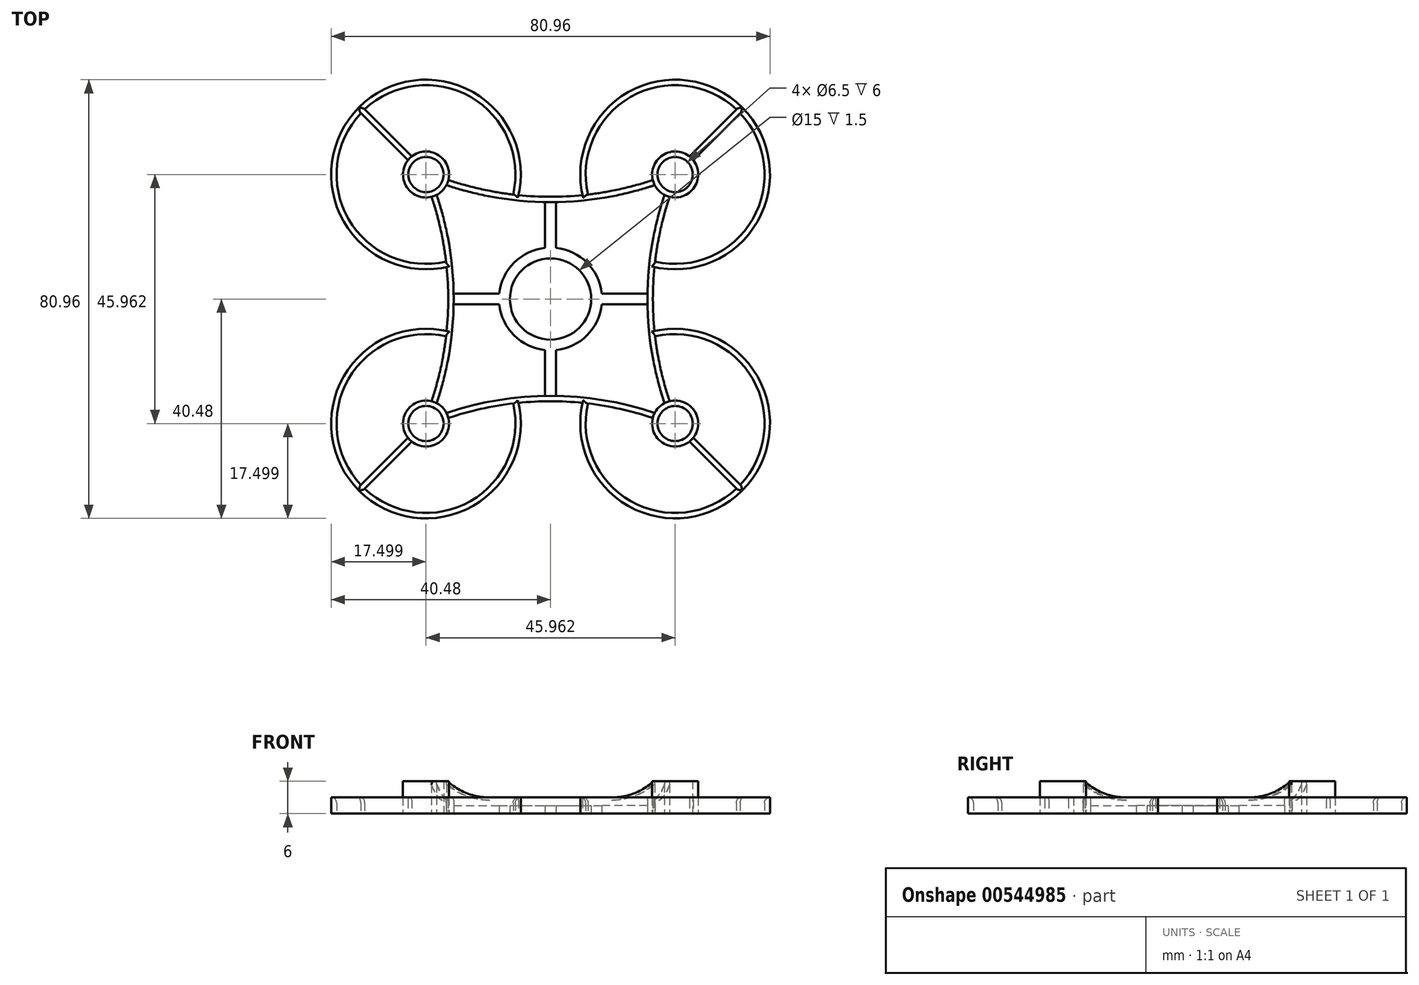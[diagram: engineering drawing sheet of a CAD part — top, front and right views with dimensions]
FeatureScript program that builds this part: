
annotation { "Feature Type Name" : "Feature", "Feature Type Description" : "" }
export const myFeature = defineFeature(function(context is Context, id is Id, definition is map)
    precondition{}
    {
        {
            var Q0;
            Q0=qCreatedBy(makeId("Top.planeOp"),FACE);
            var sketch = newSketch(context, id + "F0", { "sketchPlane" : qUnion([Q0])});
            skCircle(sketch, "E0", {"center": v(-22.98, 22.98) * mm, "radius": 3.25 * mm});
            skArc(sketch, "E1", {"start": v(-26.32, 25.61) * mm, "mid": v(-19.98, 19.98) * mm, "end": v(-25.61, 26.32) * mm});
            skLineSegment(sketch, "E2", {"start": v(0, 0) * mm, "end": v(-57.54, 57.54) * mm, "construction": true});
            skArc(sketch, "E3", {"start": v(-6.9, 19.28) * mm, "mid": v(-14.77, 37.3) * mm, "end": v(-34.29, 35) * mm});
            skArc(sketch, "E4", {"start": v(-5.9, 19.17) * mm, "mid": v(-35.36, 35.36) * mm, "end": v(-19.17, 5.9) * mm});
            skLineSegment(sketch, "E5", {"start": v(-18.38, 0) * mm, "end": v(-18.38, 18.38) * mm, "construction": true});
            skLineSegment(sketch, "E6", {"start": v(-18.38, 18.38) * mm, "end": v(0, 18.38) * mm, "construction": true});
            skArc(sketch, "E7", {"start": v(-18.38, 0) * mm, "mid": v(-19.54, 11.72) * mm, "end": v(-22.98, 22.98) * mm, "construction": true});
            skArc(sketch, "E8", {"start": v(-22.98, 22.98) * mm, "mid": v(-11.72, 19.54) * mm, "end": v(0, 18.37) * mm, "construction": true});
            skArc(sketch, "E9", {"start": v(-18.87, 0) * mm, "mid": v(-18.95, 2.95) * mm, "end": v(-19.17, 5.9) * mm});
            skArc(sketch, "E10", {"start": v(-17.88, 0) * mm, "mid": v(-18.67, 9.73) * mm, "end": v(-21.03, 19.2) * mm});
            skArc(sketch, "E11.MirrorCS", {"start": v(0, 18.87) * mm, "mid": v(-2.95, 18.95) * mm, "end": v(-5.9, 19.17) * mm});
            skArc(sketch, "E12.MirrorCS", {"start": v(0, 17.88) * mm, "mid": v(-9.73, 18.67) * mm, "end": v(-19.2, 21.03) * mm});
            skArc(sketch, "E13.trimOffspring", {"start": v(-6.9, 19.28) * mm, "mid": v(-12.95, 20.3) * mm, "end": v(-18.86, 21.96) * mm});
            skArc(sketch, "E14.trimOffspring", {"start": v(-19.28, 6.9) * mm, "mid": v(-20.3, 12.95) * mm, "end": v(-21.96, 18.86) * mm});
            skLineSegment(sketch, "E15", {"start": v(-35, 34.29) * mm, "end": v(-26.32, 25.61) * mm});
            skLineSegment(sketch, "E16.MirrorCS", {"start": v(-34.29, 35) * mm, "end": v(-25.61, 26.32) * mm});
            skArc(sketch, "E17.trimOffspring", {"start": v(-35, 34.29) * mm, "mid": v(-37.3, 14.77) * mm, "end": v(-19.28, 6.9) * mm});
            skLineSegment(sketch, "E18.MirrorCS", {"start": v(35, 34.29) * mm, "end": v(26.32, 25.61) * mm});
            skArc(sketch, "E19.MirrorCS", {"start": v(6.9, 19.28) * mm, "mid": v(12.95, 20.3) * mm, "end": v(18.86, 21.96) * mm});
            skArc(sketch, "E20.MirrorCS", {"start": v(19.28, 6.9) * mm, "mid": v(20.3, 12.95) * mm, "end": v(21.96, 18.86) * mm});
            skCircle(sketch, "E21.MirrorC", {"center": v(22.98, 22.98) * mm, "radius": 3.25 * mm});
            skArc(sketch, "E22.MirrorCS", {"start": v(26.32, 25.61) * mm, "mid": v(19.98, 19.98) * mm, "end": v(25.61, 26.32) * mm});
            skLineSegment(sketch, "E23.MirrorCS", {"start": v(0, 0) * mm, "end": v(57.54, 57.54) * mm, "construction": true});
            skArc(sketch, "E24.MirrorCS", {"start": v(5.9, 19.17) * mm, "mid": v(35.36, 35.36) * mm, "end": v(19.17, 5.9) * mm});
            skLineSegment(sketch, "E25.MirrorCS", {"start": v(18.38, 0) * mm, "end": v(18.38, 18.38) * mm, "construction": true});
            skLineSegment(sketch, "E26.MirrorCS", {"start": v(18.38, 18.38) * mm, "end": v(0, 18.38) * mm, "construction": true});
            skArc(sketch, "E27.MirrorCS", {"start": v(18.38, 0) * mm, "mid": v(19.54, 11.72) * mm, "end": v(22.98, 22.98) * mm, "construction": true});
            skArc(sketch, "E28.MirrorCS", {"start": v(22.98, 22.98) * mm, "mid": v(11.72, 19.54) * mm, "end": v(0, 18.37) * mm, "construction": true});
            skArc(sketch, "E29.MirrorCS", {"start": v(18.87, 0) * mm, "mid": v(18.95, 2.95) * mm, "end": v(19.17, 5.9) * mm});
            skArc(sketch, "E30.MirrorCS", {"start": v(17.88, 0) * mm, "mid": v(18.67, 9.73) * mm, "end": v(21.03, 19.2) * mm});
            skArc(sketch, "E31.MirrorCS", {"start": v(0, 18.87) * mm, "mid": v(2.95, 18.95) * mm, "end": v(5.9, 19.17) * mm});
            skLineSegment(sketch, "E32.MirrorCS", {"start": v(34.29, 35) * mm, "end": v(25.61, 26.32) * mm});
            skArc(sketch, "E33.MirrorCS", {"start": v(35, 34.29) * mm, "mid": v(37.3, 14.77) * mm, "end": v(19.28, 6.9) * mm});
            skArc(sketch, "E34.MirrorCS", {"start": v(6.9, 19.28) * mm, "mid": v(14.77, 37.3) * mm, "end": v(34.29, 35) * mm});
            skArc(sketch, "E35.MirrorCS", {"start": v(0, 17.88) * mm, "mid": v(9.73, 18.67) * mm, "end": v(19.2, 21.03) * mm});
            skArc(sketch, "E36.MirrorCS", {"start": v(18.87, 0) * mm, "mid": v(18.95, -2.95) * mm, "end": v(19.17, -5.9) * mm});
            skArc(sketch, "E37.MirrorCS", {"start": v(0, -18.87) * mm, "mid": v(-2.95, -18.95) * mm, "end": v(-5.9, -19.17) * mm});
            skArc(sketch, "E38.MirrorCS", {"start": v(-17.88, 0) * mm, "mid": v(-18.67, -9.73) * mm, "end": v(-21.03, -19.2) * mm});
            skArc(sketch, "E39.MirrorCS", {"start": v(0, -18.87) * mm, "mid": v(2.95, -18.95) * mm, "end": v(5.9, -19.17) * mm});
            skArc(sketch, "E40.MirrorCS", {"start": v(-18.87, 0) * mm, "mid": v(-18.95, -2.95) * mm, "end": v(-19.17, -5.9) * mm});
            skArc(sketch, "E41.MirrorCS", {"start": v(0, -17.88) * mm, "mid": v(9.73, -18.67) * mm, "end": v(19.2, -21.03) * mm});
            skArc(sketch, "E42.MirrorCS", {"start": v(-18.38, 0) * mm, "mid": v(-19.54, -11.72) * mm, "end": v(-22.98, -22.98) * mm, "construction": true});
            skLineSegment(sketch, "E43.MirrorCS", {"start": v(-18.38, 0) * mm, "end": v(-18.38, -18.38) * mm, "construction": true});
            skLineSegment(sketch, "E44.MirrorCS", {"start": v(-35, -34.29) * mm, "end": v(-26.32, -25.61) * mm});
            skCircle(sketch, "E45.MirrorC", {"center": v(22.98, -22.98) * mm, "radius": 3.25 * mm});
            skArc(sketch, "E46.MirrorCS", {"start": v(17.88, 0) * mm, "mid": v(18.67, -9.73) * mm, "end": v(21.03, -19.2) * mm});
            skArc(sketch, "E47.MirrorCS", {"start": v(-19.28, -6.9) * mm, "mid": v(-20.3, -12.95) * mm, "end": v(-21.96, -18.86) * mm});
            skArc(sketch, "E48.MirrorCS", {"start": v(-6.9, -19.28) * mm, "mid": v(-12.95, -20.3) * mm, "end": v(-18.86, -21.96) * mm});
            skLineSegment(sketch, "E49.MirrorCS", {"start": v(18.38, -18.38) * mm, "end": v(0, -18.38) * mm, "construction": true});
            skLineSegment(sketch, "E50.MirrorCS", {"start": v(0, 0) * mm, "end": v(57.54, -57.54) * mm, "construction": true});
            skArc(sketch, "E51.MirrorCS", {"start": v(0, -17.88) * mm, "mid": v(-9.73, -18.67) * mm, "end": v(-19.2, -21.03) * mm});
            skArc(sketch, "E52.MirrorCS", {"start": v(6.9, -19.28) * mm, "mid": v(12.95, -20.3) * mm, "end": v(18.86, -21.96) * mm});
            skArc(sketch, "E53.MirrorCS", {"start": v(-22.98, -22.98) * mm, "mid": v(-11.72, -19.54) * mm, "end": v(0, -18.37) * mm, "construction": true});
            skLineSegment(sketch, "E54.MirrorCS", {"start": v(-18.38, -18.38) * mm, "end": v(0, -18.38) * mm, "construction": true});
            skArc(sketch, "E55.MirrorCS", {"start": v(-5.9, -19.17) * mm, "mid": v(-35.36, -35.36) * mm, "end": v(-19.17, -5.9) * mm});
            skArc(sketch, "E56.MirrorCS", {"start": v(-6.9, -19.28) * mm, "mid": v(-14.77, -37.3) * mm, "end": v(-34.29, -35) * mm});
            skArc(sketch, "E57.MirrorCS", {"start": v(19.28, -6.9) * mm, "mid": v(20.3, -12.95) * mm, "end": v(21.96, -18.86) * mm});
            skLineSegment(sketch, "E58.MirrorCS", {"start": v(0, 0) * mm, "end": v(-57.54, -57.54) * mm, "construction": true});
            skArc(sketch, "E59.MirrorCS", {"start": v(-26.32, -25.61) * mm, "mid": v(-19.98, -19.98) * mm, "end": v(-25.61, -26.32) * mm});
            skArc(sketch, "E60.MirrorCS", {"start": v(18.38, 0) * mm, "mid": v(19.54, -11.72) * mm, "end": v(22.98, -22.98) * mm, "construction": true});
            skLineSegment(sketch, "E61.MirrorCS", {"start": v(34.29, -35) * mm, "end": v(25.61, -26.32) * mm});
            skLineSegment(sketch, "E62.MirrorCS", {"start": v(-34.29, -35) * mm, "end": v(-25.61, -26.32) * mm});
            skArc(sketch, "E63.MirrorCS", {"start": v(22.98, -22.98) * mm, "mid": v(11.72, -19.54) * mm, "end": v(0, -18.37) * mm, "construction": true});
            skArc(sketch, "E64.MirrorCS", {"start": v(5.9, -19.17) * mm, "mid": v(35.36, -35.36) * mm, "end": v(19.17, -5.9) * mm});
            skArc(sketch, "E65.MirrorCS", {"start": v(-35, -34.29) * mm, "mid": v(-37.3, -14.77) * mm, "end": v(-19.28, -6.9) * mm});
            skCircle(sketch, "E66.MirrorC", {"center": v(-22.98, -22.98) * mm, "radius": 3.25 * mm});
            skArc(sketch, "E67.MirrorCS", {"start": v(35, -34.29) * mm, "mid": v(37.3, -14.77) * mm, "end": v(19.28, -6.9) * mm});
            skArc(sketch, "E68.MirrorCS", {"start": v(26.32, -25.61) * mm, "mid": v(19.98, -19.98) * mm, "end": v(25.61, -26.32) * mm});
            skLineSegment(sketch, "E69.MirrorCS", {"start": v(18.38, 0) * mm, "end": v(18.38, -18.38) * mm, "construction": true});
            skLineSegment(sketch, "E70.MirrorCS", {"start": v(35, -34.29) * mm, "end": v(26.32, -25.61) * mm});
            skArc(sketch, "E71.MirrorCS", {"start": v(6.9, -19.28) * mm, "mid": v(14.77, -37.3) * mm, "end": v(34.29, -35) * mm});
            skSolve(sketch);
        }
        {
            var Q0;
            Q0 = qSketchRegion(id + "F0", true);
            extrude(context, id + "F1", {"entities" : qUnion([Q0]), "depth" : 3 * mm, "offsetDistance" : 25 * mm});
        }
        {
            var Q0;
            Q0=makeQuery(id+"F1.opExtrude","CAP_FACE",FACE,{"disambiguationData":[OSD([sQuery(id+"F0.wireOp",EDGE,"E0"),sQuery(id+"F0.wireOp",EDGE,"E1"),sQuery(id+"F0.wireOp",EDGE,"E3"),sQuery(id+"F0.wireOp",EDGE,"E4"),sQuery(id+"F0.wireOp",EDGE,"E9"),sQuery(id+"F0.wireOp",EDGE,"E10"),sQuery(id+"F0.wireOp",EDGE,"E11.MirrorCS"),sQuery(id+"F0.wireOp",EDGE,"E12.MirrorCS"),sQuery(id+"F0.wireOp",EDGE,"E13.trimOffspring"),sQuery(id+"F0.wireOp",EDGE,"E14.trimOffspring"),sQuery(id+"F0.wireOp",EDGE,"E15"),sQuery(id+"F0.wireOp",EDGE,"E16.MirrorCS"),sQuery(id+"F0.wireOp",EDGE,"E17.trimOffspring"),sQuery(id+"F0.wireOp",EDGE,"E18.MirrorCS"),sQuery(id+"F0.wireOp",EDGE,"E19.MirrorCS"),sQuery(id+"F0.wireOp",EDGE,"E20.MirrorCS"),sQuery(id+"F0.wireOp",EDGE,"E21.MirrorC"),sQuery(id+"F0.wireOp",EDGE,"E22.MirrorCS"),sQuery(id+"F0.wireOp",EDGE,"E24.MirrorCS"),sQuery(id+"F0.wireOp",EDGE,"E29.MirrorCS"),sQuery(id+"F0.wireOp",EDGE,"E30.MirrorCS"),sQuery(id+"F0.wireOp",EDGE,"E31.MirrorCS"),sQuery(id+"F0.wireOp",EDGE,"E32.MirrorCS"),sQuery(id+"F0.wireOp",EDGE,"E33.MirrorCS"),sQuery(id+"F0.wireOp",EDGE,"E34.MirrorCS"),sQuery(id+"F0.wireOp",EDGE,"E35.MirrorCS"),sQuery(id+"F0.wireOp",EDGE,"E36.MirrorCS"),sQuery(id+"F0.wireOp",EDGE,"E37.MirrorCS"),sQuery(id+"F0.wireOp",EDGE,"E38.MirrorCS"),sQuery(id+"F0.wireOp",EDGE,"E39.MirrorCS"),sQuery(id+"F0.wireOp",EDGE,"E40.MirrorCS"),sQuery(id+"F0.wireOp",EDGE,"E41.MirrorCS"),sQuery(id+"F0.wireOp",EDGE,"E44.MirrorCS"),sQuery(id+"F0.wireOp",EDGE,"E45.MirrorC"),sQuery(id+"F0.wireOp",EDGE,"E46.MirrorCS"),sQuery(id+"F0.wireOp",EDGE,"E47.MirrorCS"),sQuery(id+"F0.wireOp",EDGE,"E48.MirrorCS"),sQuery(id+"F0.wireOp",EDGE,"E51.MirrorCS"),sQuery(id+"F0.wireOp",EDGE,"E52.MirrorCS"),sQuery(id+"F0.wireOp",EDGE,"E55.MirrorCS"),sQuery(id+"F0.wireOp",EDGE,"E56.MirrorCS"),sQuery(id+"F0.wireOp",EDGE,"E57.MirrorCS"),sQuery(id+"F0.wireOp",EDGE,"E59.MirrorCS"),sQuery(id+"F0.wireOp",EDGE,"E61.MirrorCS"),sQuery(id+"F0.wireOp",EDGE,"E62.MirrorCS"),sQuery(id+"F0.wireOp",EDGE,"E64.MirrorCS"),sQuery(id+"F0.wireOp",EDGE,"E65.MirrorCS"),sQuery(id+"F0.wireOp",EDGE,"E66.MirrorC"),sQuery(id+"F0.wireOp",EDGE,"E67.MirrorCS"),sQuery(id+"F0.wireOp",EDGE,"E68.MirrorCS"),sQuery(id+"F0.wireOp",EDGE,"E70.MirrorCS"),sQuery(id+"F0.wireOp",EDGE,"E71.MirrorCS")])],"isStart":true});
            var sketch = newSketch(context, id + "F2", { "sketchPlane" : qUnion([Q0])});
            skCircle(sketch, "E72", {"center": v(0, 0) * mm, "radius": 7.5 * mm});
            skArc(sketch, "E73", {"start": v(-9.45, -1) * mm, "mid": v(-6.72, -6.72) * mm, "end": v(-1, -9.45) * mm});
            skLineSegment(sketch, "E74", {"start": v(-17.88, -1) * mm, "end": v(-9.45, -1) * mm});
            skLineSegment(sketch, "E75.MirrorCS", {"start": v(-17.88, 1) * mm, "end": v(-9.45, 1) * mm});
            skLineSegment(sketch, "E76.1.0", {"start": v(-1, -17.88) * mm, "end": v(-1, -9.45) * mm});
            skLineSegment(sketch, "E76.1.1", {"start": v(1, -17.88) * mm, "end": v(1, -9.45) * mm});
            skLineSegment(sketch, "E76.2.0", {"start": v(17.88, -1) * mm, "end": v(9.45, -1) * mm});
            skLineSegment(sketch, "E76.2.1", {"start": v(17.88, 1) * mm, "end": v(9.45, 1) * mm});
            skLineSegment(sketch, "E76.3.0", {"start": v(1, 17.88) * mm, "end": v(1, 9.45) * mm});
            skLineSegment(sketch, "E76.3.1", {"start": v(-1, 17.88) * mm, "end": v(-1, 9.45) * mm});
            skArc(sketch, "E77.trimOffspring", {"start": v(-1, 9.45) * mm, "mid": v(-6.72, 6.72) * mm, "end": v(-9.45, 1) * mm});
            skArc(sketch, "E78.trimOffspring", {"start": v(9.45, 1) * mm, "mid": v(6.72, 6.72) * mm, "end": v(1, 9.45) * mm});
            skArc(sketch, "E79.trimOffspring", {"start": v(1, -9.45) * mm, "mid": v(6.72, -6.72) * mm, "end": v(9.45, -1) * mm});
            skSolve(sketch);
        }
        {
            var Q0;
            Q0=makeQuery(id+"F2.imprint","IMPRINT",FACE,{"disambiguationData":[TD([[makeQuery(id+"F2.imprint","IMPRINT",EDGE,{"derivedFrom":sQuery(id+"F2.wireOp",EDGE,"E72")}),-1.0]])]});
            extrude(context, id + "F3", {"entities" : qUnion([Q0]), "operationType" : NewBodyOperationType.ADD, "oppositeDirection" : true, "depth" : 1.5 * mm, "offsetDistance" : 25 * mm});
        }
        {
            var Q0;
            Q0=makeQuery(id+"F1.opExtrude","CAP_EDGE",EDGE,{"disambiguationData":[OSD([sQuery(id+"F0.wireOp",EDGE,"E17.trimOffspring")])],"isStart":false});
            var Q1;
            Q1=makeQuery(id+"F1.opExtrude","CAP_EDGE",EDGE,{"disambiguationData":[OSD([sQuery(id+"F0.wireOp",EDGE,"E3")])],"isStart":false});
            var Q2;
            Q2=makeQuery(id+"F1.opExtrude","CAP_EDGE",EDGE,{"disambiguationData":[OSD([sQuery(id+"F0.wireOp",EDGE,"E65.MirrorCS")])],"isStart":false});
            var Q3;
            Q3=makeQuery(id+"F1.opExtrude","CAP_EDGE",EDGE,{"disambiguationData":[OSD([sQuery(id+"F0.wireOp",EDGE,"E56.MirrorCS")])],"isStart":false});
            var Q4;
            Q4=makeQuery(id+"F1.opExtrude","CAP_EDGE",EDGE,{"disambiguationData":[OSD([sQuery(id+"F0.wireOp",EDGE,"E71.MirrorCS")])],"isStart":false});
            var Q5;
            Q5=makeQuery(id+"F1.opExtrude","CAP_EDGE",EDGE,{"disambiguationData":[OSD([sQuery(id+"F0.wireOp",EDGE,"E67.MirrorCS")])],"isStart":false});
            var Q6;
            Q6=makeQuery(id+"F1.opExtrude","CAP_EDGE",EDGE,{"disambiguationData":[OSD([sQuery(id+"F0.wireOp",EDGE,"E34.MirrorCS")])],"isStart":false});
            var Q7;
            Q7=makeQuery(id+"F1.opExtrude","CAP_EDGE",EDGE,{"disambiguationData":[OSD([sQuery(id+"F0.wireOp",EDGE,"E33.MirrorCS")])],"isStart":false});
            fillet(context, id + "F4", {"entities" : qUnion([Q0, Q1, Q2, Q3, Q4, Q5, Q6, Q7]), "radius" : 1 * mm, "tangentPropagation" : true, "allowEdgeOverflow" : false});
        }
        {
            var Q0;
            Q0=makeQuery(id+"F1.opExtrude","CAP_EDGE",EDGE,{"disambiguationData":[OSD([sQuery(id+"F0.wireOp",EDGE,"E15")])],"isStart":false});
            var Q1;
            Q1=makeQuery(id+"F1.opExtrude","CAP_EDGE",EDGE,{"disambiguationData":[OSD([sQuery(id+"F0.wireOp",EDGE,"E16.MirrorCS")])],"isStart":false});
            var Q2;
            Q2=makeQuery(id+"F1.opExtrude","CAP_EDGE",EDGE,{"disambiguationData":[OSD([sQuery(id+"F0.wireOp",EDGE,"E62.MirrorCS")])],"isStart":false});
            var Q3;
            Q3=makeQuery(id+"F1.opExtrude","CAP_EDGE",EDGE,{"disambiguationData":[OSD([sQuery(id+"F0.wireOp",EDGE,"E44.MirrorCS")])],"isStart":false});
            var Q4;
            Q4=makeQuery(id+"F1.opExtrude","CAP_EDGE",EDGE,{"disambiguationData":[OSD([sQuery(id+"F0.wireOp",EDGE,"E18.MirrorCS")])],"isStart":false});
            var Q5;
            Q5=makeQuery(id+"F1.opExtrude","CAP_EDGE",EDGE,{"disambiguationData":[OSD([sQuery(id+"F0.wireOp",EDGE,"E32.MirrorCS")])],"isStart":false});
            var Q6;
            Q6=makeQuery(id+"F1.opExtrude","CAP_EDGE",EDGE,{"disambiguationData":[OSD([sQuery(id+"F0.wireOp",EDGE,"E70.MirrorCS")])],"isStart":false});
            var Q7;
            Q7=makeQuery(id+"F1.opExtrude","CAP_EDGE",EDGE,{"disambiguationData":[OSD([sQuery(id+"F0.wireOp",EDGE,"E61.MirrorCS")])],"isStart":false});
            fillet(context, id + "F5", {"entities" : qUnion([Q0, Q1, Q2, Q3, Q4, Q5, Q6, Q7]), "radius" : .5 * mm, "tangentPropagation" : true, "allowEdgeOverflow" : false});
        }
        {
            var Q0;
            Q0=makeQuery(id+"F1.opExtrude","CAP_FACE",FACE,{"disambiguationData":[OSD([sQuery(id+"F0.wireOp",EDGE,"E0"),sQuery(id+"F0.wireOp",EDGE,"E1"),sQuery(id+"F0.wireOp",EDGE,"E3"),sQuery(id+"F0.wireOp",EDGE,"E4"),sQuery(id+"F0.wireOp",EDGE,"E9"),sQuery(id+"F0.wireOp",EDGE,"E10"),sQuery(id+"F0.wireOp",EDGE,"E11.MirrorCS"),sQuery(id+"F0.wireOp",EDGE,"E12.MirrorCS"),sQuery(id+"F0.wireOp",EDGE,"E13.trimOffspring"),sQuery(id+"F0.wireOp",EDGE,"E14.trimOffspring"),sQuery(id+"F0.wireOp",EDGE,"E15"),sQuery(id+"F0.wireOp",EDGE,"E16.MirrorCS"),sQuery(id+"F0.wireOp",EDGE,"E17.trimOffspring"),sQuery(id+"F0.wireOp",EDGE,"E18.MirrorCS"),sQuery(id+"F0.wireOp",EDGE,"E19.MirrorCS"),sQuery(id+"F0.wireOp",EDGE,"E20.MirrorCS"),sQuery(id+"F0.wireOp",EDGE,"E21.MirrorC"),sQuery(id+"F0.wireOp",EDGE,"E22.MirrorCS"),sQuery(id+"F0.wireOp",EDGE,"E24.MirrorCS"),sQuery(id+"F0.wireOp",EDGE,"E29.MirrorCS"),sQuery(id+"F0.wireOp",EDGE,"E30.MirrorCS"),sQuery(id+"F0.wireOp",EDGE,"E31.MirrorCS"),sQuery(id+"F0.wireOp",EDGE,"E32.MirrorCS"),sQuery(id+"F0.wireOp",EDGE,"E33.MirrorCS"),sQuery(id+"F0.wireOp",EDGE,"E34.MirrorCS"),sQuery(id+"F0.wireOp",EDGE,"E35.MirrorCS"),sQuery(id+"F0.wireOp",EDGE,"E36.MirrorCS"),sQuery(id+"F0.wireOp",EDGE,"E37.MirrorCS"),sQuery(id+"F0.wireOp",EDGE,"E38.MirrorCS"),sQuery(id+"F0.wireOp",EDGE,"E39.MirrorCS"),sQuery(id+"F0.wireOp",EDGE,"E40.MirrorCS"),sQuery(id+"F0.wireOp",EDGE,"E41.MirrorCS"),sQuery(id+"F0.wireOp",EDGE,"E44.MirrorCS"),sQuery(id+"F0.wireOp",EDGE,"E45.MirrorC"),sQuery(id+"F0.wireOp",EDGE,"E46.MirrorCS"),sQuery(id+"F0.wireOp",EDGE,"E47.MirrorCS"),sQuery(id+"F0.wireOp",EDGE,"E48.MirrorCS"),sQuery(id+"F0.wireOp",EDGE,"E51.MirrorCS"),sQuery(id+"F0.wireOp",EDGE,"E52.MirrorCS"),sQuery(id+"F0.wireOp",EDGE,"E55.MirrorCS"),sQuery(id+"F0.wireOp",EDGE,"E56.MirrorCS"),sQuery(id+"F0.wireOp",EDGE,"E57.MirrorCS"),sQuery(id+"F0.wireOp",EDGE,"E59.MirrorCS"),sQuery(id+"F0.wireOp",EDGE,"E61.MirrorCS"),sQuery(id+"F0.wireOp",EDGE,"E62.MirrorCS"),sQuery(id+"F0.wireOp",EDGE,"E64.MirrorCS"),sQuery(id+"F0.wireOp",EDGE,"E65.MirrorCS"),sQuery(id+"F0.wireOp",EDGE,"E66.MirrorC"),sQuery(id+"F0.wireOp",EDGE,"E67.MirrorCS"),sQuery(id+"F0.wireOp",EDGE,"E68.MirrorCS"),sQuery(id+"F0.wireOp",EDGE,"E70.MirrorCS"),sQuery(id+"F0.wireOp",EDGE,"E71.MirrorCS")])],"isStart":false});
            var sketch = newSketch(context, id + "F6", { "sketchPlane" : qUnion([Q0])});
            skCircle(sketch, "E80", {"center": v(-22.98, -22.98) * mm, "radius": 4.25 * mm});
            skCircle(sketch, "E81", {"center": v(-22.98, -22.98) * mm, "radius": 3.25 * mm});
            skCircle(sketch, "E82", {"center": v(-22.98, 22.98) * mm, "radius": 4.25 * mm});
            skCircle(sketch, "E83", {"center": v(-22.98, 22.98) * mm, "radius": 3.25 * mm});
            skCircle(sketch, "E84", {"center": v(22.98, 22.98) * mm, "radius": 4.25 * mm});
            skCircle(sketch, "E85", {"center": v(22.98, 22.98) * mm, "radius": 3.25 * mm});
            skCircle(sketch, "E86", {"center": v(22.98, -22.98) * mm, "radius": 3.25 * mm});
            skCircle(sketch, "E87", {"center": v(22.98, -22.98) * mm, "radius": 4.25 * mm});
            skSolve(sketch);
        }
        {
            var Q0;
            Q0 = qSketchRegion(id + "F6", true);
            extrude(context, id + "F7", {"entities" : qUnion([Q0]), "operationType" : NewBodyOperationType.ADD, "depth" : 3 * mm, "offsetDistance" : 25 * mm});
        }
        {
            var Q0;
            {var subQ6=sQuery(id+"F0.wireOp",EDGE,"E14.trimOffspring");var subQ8=sQuery(id+"F6.wireOp",EDGE,"E82");Q0=makeQuery(id+"F7.boolean.opBoolean","SPLIT",EDGE,{"disambiguationData":[TD([makeQuery(id+"F1.opExtrude","SWEPT_FACE",FACE,{"disambiguationData":[OSD([subQ6])]})])],"derivedFrom":makeQuery(id+"F7.opExtrude","CAP_EDGE",EDGE,{"disambiguationData":[OSD([subQ8])],"isStart":true})});}
            var Q1;
            {var subQ2=sQuery(id+"F0.wireOp",EDGE,"E13.trimOffspring");var subQ8=sQuery(id+"F6.wireOp",EDGE,"E82");Q1=makeQuery(id+"F7.boolean.opBoolean","SPLIT",EDGE,{"disambiguationData":[TD([makeQuery(id+"F1.opExtrude","SWEPT_FACE",FACE,{"disambiguationData":[OSD([subQ2])]})])],"derivedFrom":makeQuery(id+"F7.opExtrude","CAP_EDGE",EDGE,{"disambiguationData":[OSD([subQ8])],"isStart":true})});}
            var Q2;
            {var subQ0=sQuery(id+"F0.wireOp",EDGE,"E19.MirrorCS");var subQ7=sQuery(id+"F6.wireOp",EDGE,"E84");Q2=makeQuery(id+"F7.boolean.opBoolean","SPLIT",EDGE,{"disambiguationData":[TD([makeQuery(id+"F1.opExtrude","SWEPT_FACE",FACE,{"disambiguationData":[OSD([subQ0])]})])],"derivedFrom":makeQuery(id+"F7.opExtrude","CAP_EDGE",EDGE,{"disambiguationData":[OSD([subQ7])],"isStart":true})});}
            var Q3;
            {var subQ2=sQuery(id+"F0.wireOp",EDGE,"E20.MirrorCS");var subQ5=sQuery(id+"F6.wireOp",EDGE,"E84");Q3=makeQuery(id+"F7.boolean.opBoolean","SPLIT",EDGE,{"disambiguationData":[TD([makeQuery(id+"F1.opExtrude","SWEPT_FACE",FACE,{"disambiguationData":[OSD([subQ2])]})])],"derivedFrom":makeQuery(id+"F7.opExtrude","CAP_EDGE",EDGE,{"disambiguationData":[OSD([subQ5])],"isStart":true})});}
            var Q4;
            {var subQ1=sQuery(id+"F0.wireOp",EDGE,"E57.MirrorCS");var subQ8=sQuery(id+"F6.wireOp",EDGE,"E87");Q4=makeQuery(id+"F7.boolean.opBoolean","SPLIT",EDGE,{"disambiguationData":[TD([makeQuery(id+"F1.opExtrude","SWEPT_FACE",FACE,{"disambiguationData":[OSD([subQ1])]})])],"derivedFrom":makeQuery(id+"F7.opExtrude","CAP_EDGE",EDGE,{"disambiguationData":[OSD([subQ8])],"isStart":true})});}
            var Q5;
            {var subQ3=sQuery(id+"F0.wireOp",EDGE,"E52.MirrorCS");var subQ8=sQuery(id+"F6.wireOp",EDGE,"E87");Q5=makeQuery(id+"F7.boolean.opBoolean","SPLIT",EDGE,{"disambiguationData":[TD([makeQuery(id+"F1.opExtrude","SWEPT_FACE",FACE,{"disambiguationData":[OSD([subQ3])]})])],"derivedFrom":makeQuery(id+"F7.opExtrude","CAP_EDGE",EDGE,{"disambiguationData":[OSD([subQ8])],"isStart":true})});}
            var Q6;
            {var subQ3=sQuery(id+"F0.wireOp",EDGE,"E48.MirrorCS");var subQ8=sQuery(id+"F6.wireOp",EDGE,"E80");Q6=makeQuery(id+"F7.boolean.opBoolean","SPLIT",EDGE,{"disambiguationData":[TD([makeQuery(id+"F1.opExtrude","SWEPT_FACE",FACE,{"disambiguationData":[OSD([subQ3])]})])],"derivedFrom":makeQuery(id+"F7.opExtrude","CAP_EDGE",EDGE,{"disambiguationData":[OSD([subQ8])],"isStart":true})});}
            var Q7;
            {var subQ2=sQuery(id+"F0.wireOp",EDGE,"E47.MirrorCS");var subQ8=sQuery(id+"F6.wireOp",EDGE,"E80");Q7=makeQuery(id+"F7.boolean.opBoolean","SPLIT",EDGE,{"disambiguationData":[TD([makeQuery(id+"F1.opExtrude","SWEPT_FACE",FACE,{"disambiguationData":[OSD([subQ2])]})])],"derivedFrom":makeQuery(id+"F7.opExtrude","CAP_EDGE",EDGE,{"disambiguationData":[OSD([subQ8])],"isStart":true})});}
            fillet(context, id + "F8", {"entities" : qUnion([Q0, Q1, Q2, Q3, Q4, Q5, Q6, Q7]), "radius" : 12 * mm, "tangentPropagation" : true, "allowEdgeOverflow" : false});
        }
        {
            var Q0;
            {var subQ0=sQuery(id+"F0.wireOp",EDGE,"E19.MirrorCS");var subQ1=makeQuery(id+"F1.opExtrude","SWEPT_FACE",FACE,{"disambiguationData":[OSD([subQ0])]});var subQ8=sQuery(id+"F6.wireOp",EDGE,"E84");Q0=makeQuery(id+"F8.opFillet","BLEND_EDGE",EDGE,{"blendedFrom":[makeQuery(id+"F7.boolean.opBoolean","SPLIT",EDGE,{"disambiguationData":[TD([subQ1])],"derivedFrom":makeQuery(id+"F7.opExtrude","CAP_EDGE",EDGE,{"disambiguationData":[OSD([subQ8])],"isStart":true})}),subQ1],"blendedInto":[subQ1]});}
            var Q1;
            {var subQ0=sQuery(id+"F0.wireOp",EDGE,"E35.MirrorCS");var subQ1=sQuery(id+"F0.wireOp",EDGE,"E12.MirrorCS");var subQ2=makeQuery(id+"F1.opExtrude","SWEPT_FACE",FACE,{"disambiguationData":[OSD([subQ1,subQ0])]});var subQ3=sQuery(id+"F0.wireOp",EDGE,"E19.MirrorCS");var subQ8=sQuery(id+"F6.wireOp",EDGE,"E84");Q1=makeQuery(id+"F8.opFillet","BLEND_EDGE",EDGE,{"blendedFrom":[makeQuery(id+"F7.boolean.opBoolean","SPLIT",EDGE,{"disambiguationData":[TD([makeQuery(id+"F1.opExtrude","SWEPT_FACE",FACE,{"disambiguationData":[OSD([subQ3])]})])],"derivedFrom":makeQuery(id+"F7.opExtrude","CAP_EDGE",EDGE,{"disambiguationData":[OSD([subQ8])],"isStart":true})}),subQ2],"blendedInto":[subQ2]});}
            var Q2;
            {var subQ0=sQuery(id+"F0.wireOp",EDGE,"E46.MirrorCS");var subQ1=sQuery(id+"F0.wireOp",EDGE,"E30.MirrorCS");var subQ2=makeQuery(id+"F1.opExtrude","SWEPT_FACE",FACE,{"disambiguationData":[OSD([subQ1,subQ0])]});var subQ5=sQuery(id+"F0.wireOp",EDGE,"E20.MirrorCS");var subQ7=sQuery(id+"F6.wireOp",EDGE,"E84");Q2=makeQuery(id+"F8.opFillet","BLEND_EDGE",EDGE,{"blendedFrom":[makeQuery(id+"F7.boolean.opBoolean","SPLIT",EDGE,{"disambiguationData":[TD([makeQuery(id+"F1.opExtrude","SWEPT_FACE",FACE,{"disambiguationData":[OSD([subQ5])]})])],"derivedFrom":makeQuery(id+"F7.opExtrude","CAP_EDGE",EDGE,{"disambiguationData":[OSD([subQ7])],"isStart":true})}),subQ2],"blendedInto":[subQ2]});}
            var Q3;
            {var subQ0=sQuery(id+"F0.wireOp",EDGE,"E20.MirrorCS");var subQ1=makeQuery(id+"F1.opExtrude","SWEPT_FACE",FACE,{"disambiguationData":[OSD([subQ0])]});var subQ6=sQuery(id+"F6.wireOp",EDGE,"E84");Q3=makeQuery(id+"F8.opFillet","BLEND_EDGE",EDGE,{"blendedFrom":[makeQuery(id+"F7.boolean.opBoolean","SPLIT",EDGE,{"disambiguationData":[TD([subQ1])],"derivedFrom":makeQuery(id+"F7.opExtrude","CAP_EDGE",EDGE,{"disambiguationData":[OSD([subQ6])],"isStart":true})}),subQ1],"blendedInto":[subQ1]});}
            var Q4;
            {var subQ0=sQuery(id+"F0.wireOp",EDGE,"E57.MirrorCS");var subQ1=makeQuery(id+"F1.opExtrude","SWEPT_FACE",FACE,{"disambiguationData":[OSD([subQ0])]});var subQ9=sQuery(id+"F6.wireOp",EDGE,"E87");Q4=makeQuery(id+"F8.opFillet","BLEND_EDGE",EDGE,{"blendedFrom":[makeQuery(id+"F7.boolean.opBoolean","SPLIT",EDGE,{"disambiguationData":[TD([subQ1])],"derivedFrom":makeQuery(id+"F7.opExtrude","CAP_EDGE",EDGE,{"disambiguationData":[OSD([subQ9])],"isStart":true})}),subQ1],"blendedInto":[subQ1]});}
            var Q5;
            {var subQ0=sQuery(id+"F0.wireOp",EDGE,"E51.MirrorCS");var subQ1=sQuery(id+"F0.wireOp",EDGE,"E41.MirrorCS");var subQ2=makeQuery(id+"F1.opExtrude","SWEPT_FACE",FACE,{"disambiguationData":[OSD([subQ1,subQ0])]});var subQ6=sQuery(id+"F0.wireOp",EDGE,"E52.MirrorCS");var subQ9=sQuery(id+"F6.wireOp",EDGE,"E87");Q5=makeQuery(id+"F8.opFillet","BLEND_EDGE",EDGE,{"blendedFrom":[makeQuery(id+"F7.boolean.opBoolean","SPLIT",EDGE,{"disambiguationData":[TD([makeQuery(id+"F1.opExtrude","SWEPT_FACE",FACE,{"disambiguationData":[OSD([subQ6])]})])],"derivedFrom":makeQuery(id+"F7.opExtrude","CAP_EDGE",EDGE,{"disambiguationData":[OSD([subQ9])],"isStart":true})}),subQ2],"blendedInto":[subQ2]});}
            var Q6;
            {var subQ0=sQuery(id+"F0.wireOp",EDGE,"E48.MirrorCS");var subQ1=makeQuery(id+"F1.opExtrude","SWEPT_FACE",FACE,{"disambiguationData":[OSD([subQ0])]});var subQ9=sQuery(id+"F6.wireOp",EDGE,"E80");Q6=makeQuery(id+"F8.opFillet","BLEND_EDGE",EDGE,{"blendedFrom":[makeQuery(id+"F7.boolean.opBoolean","SPLIT",EDGE,{"disambiguationData":[TD([subQ1])],"derivedFrom":makeQuery(id+"F7.opExtrude","CAP_EDGE",EDGE,{"disambiguationData":[OSD([subQ9])],"isStart":true})}),subQ1],"blendedInto":[subQ1]});}
            var Q7;
            {var subQ0=sQuery(id+"F0.wireOp",EDGE,"E14.trimOffspring");var subQ1=makeQuery(id+"F1.opExtrude","SWEPT_FACE",FACE,{"disambiguationData":[OSD([subQ0])]});var subQ9=sQuery(id+"F6.wireOp",EDGE,"E82");Q7=makeQuery(id+"F8.opFillet","BLEND_EDGE",EDGE,{"blendedFrom":[makeQuery(id+"F7.boolean.opBoolean","SPLIT",EDGE,{"disambiguationData":[TD([subQ1])],"derivedFrom":makeQuery(id+"F7.opExtrude","CAP_EDGE",EDGE,{"disambiguationData":[OSD([subQ9])],"isStart":true})}),subQ1],"blendedInto":[subQ1]});}
            var Q8;
            {var subQ0=sQuery(id+"F0.wireOp",EDGE,"E47.MirrorCS");var subQ1=makeQuery(id+"F1.opExtrude","SWEPT_FACE",FACE,{"disambiguationData":[OSD([subQ0])]});var subQ9=sQuery(id+"F6.wireOp",EDGE,"E80");Q8=makeQuery(id+"F8.opFillet","BLEND_EDGE",EDGE,{"blendedFrom":[makeQuery(id+"F7.boolean.opBoolean","SPLIT",EDGE,{"disambiguationData":[TD([subQ1])],"derivedFrom":makeQuery(id+"F7.opExtrude","CAP_EDGE",EDGE,{"disambiguationData":[OSD([subQ9])],"isStart":true})}),subQ1],"blendedInto":[subQ1]});}
            var Q9;
            Q9=makeQuery(id+"F1.opExtrude","CAP_EDGE",EDGE,{"disambiguationData":[OSD([sQuery(id+"F0.wireOp",EDGE,"E10"),sQuery(id+"F0.wireOp",EDGE,"E38.MirrorCS")])],"isStart":false});
            var Q10;
            {var subQ0=sQuery(id+"F0.wireOp",EDGE,"E13.trimOffspring");var subQ1=makeQuery(id+"F1.opExtrude","SWEPT_FACE",FACE,{"disambiguationData":[OSD([subQ0])]});var subQ9=sQuery(id+"F6.wireOp",EDGE,"E82");Q10=makeQuery(id+"F8.opFillet","BLEND_EDGE",EDGE,{"blendedFrom":[makeQuery(id+"F7.boolean.opBoolean","SPLIT",EDGE,{"disambiguationData":[TD([subQ1])],"derivedFrom":makeQuery(id+"F7.opExtrude","CAP_EDGE",EDGE,{"disambiguationData":[OSD([subQ9])],"isStart":true})}),subQ1],"blendedInto":[subQ1]});}
            var Q11;
            Q11=makeQuery(id+"F1.opExtrude","CAP_EDGE",EDGE,{"disambiguationData":[OSD([sQuery(id+"F0.wireOp",EDGE,"E52.MirrorCS")])],"isStart":false});
            fillet(context, id + "F9", {"entities" : qUnion([Q0, Q1, Q2, Q3, Q4, Q5, Q6, Q7, Q8, Q9, Q10, Q11]), "radius" : .5 * mm, "tangentPropagation" : true, "allowEdgeOverflow" : false});
        }
    });
